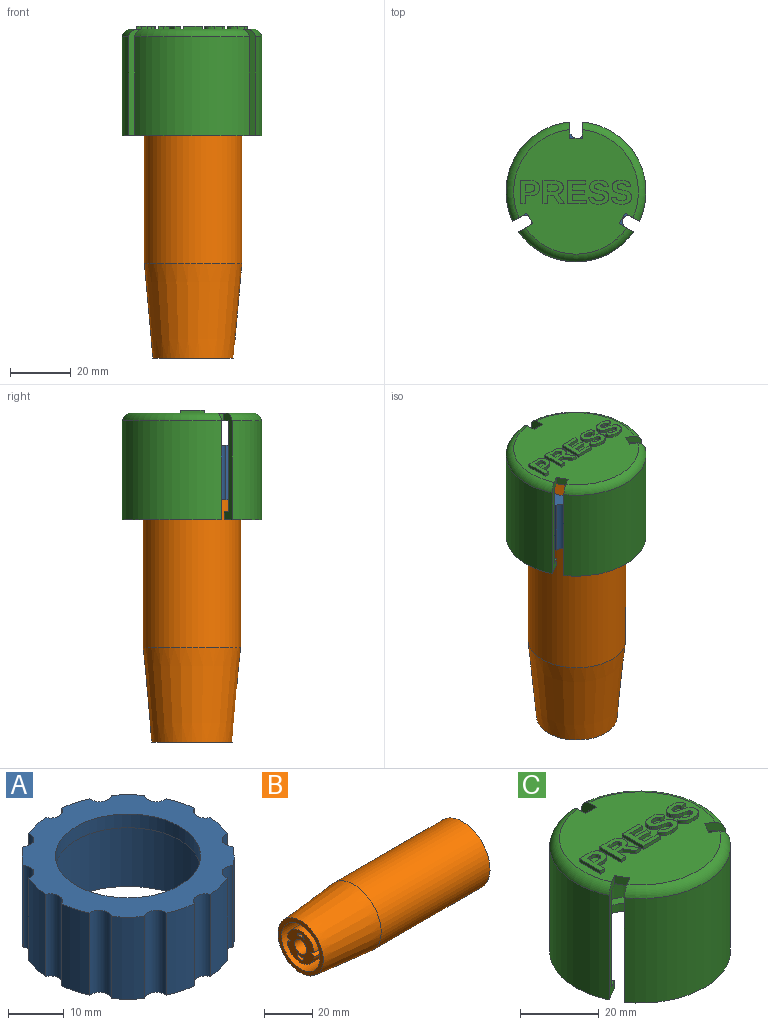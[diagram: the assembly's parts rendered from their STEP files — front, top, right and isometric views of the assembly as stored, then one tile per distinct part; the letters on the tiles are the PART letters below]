
ASSEMBLY  parts=3 mates=1
PART A: 29 faces, bbox 37.8x37.8x18 mm
  f0: plane 32x32mm, normal (0,0,-1), area 273.3mm2, adj f25,f27
  f1: cylinder r=2.13mm len=18mm, axis (0,0,-1), area 93.4mm2, adj f2,f24,f26,f28
  f2: cylinder r=19mm len=18mm, axis (0,0,-1), area 106.9mm2, adj f1,f3,f26,f28
  f3: cylinder r=2.13mm len=18mm, axis (0,0,-1), area 93.4mm2, adj f2,f4,f26,f28
  f4: cylinder r=19mm len=18mm, axis (0,0,-1), area 106.9mm2, adj f3,f5,f26,f28
  f5: cylinder r=2.13mm len=18mm, axis (0,0,-1), area 93.4mm2, adj f4,f6,f26,f28
  f6: cylinder r=19mm len=18mm, axis (0,0,-1), area 106.9mm2, adj f5,f7,f26,f28
  f7: cylinder r=2.13mm len=18mm, axis (0,0,-1), area 93.4mm2, adj f6,f8,f26,f28
  f8: cylinder r=19mm len=18mm, axis (0,0,-1), area 106.9mm2, adj f7,f9,f26,f28
  f9: cylinder r=2.13mm len=18mm, axis (0,0,-1), area 93.4mm2, adj f8,f10,f26,f28
  f10: cylinder r=19mm len=18mm, axis (0,0,-1), area 106.9mm2, adj f9,f11,f26,f28
  f11: cylinder r=2.13mm len=18mm, axis (0,0,-1), area 93.4mm2, adj f10,f12,f26,f28
  f12: cylinder r=19mm len=18mm, axis (0,0,-1), area 106.9mm2, adj f11,f13,f26,f28
  f13: cylinder r=2.13mm len=18mm, axis (0,0,-1), area 93.4mm2, adj f12,f14,f26,f28
  f14: cylinder r=19mm len=18mm, axis (0,0,-1), area 106.9mm2, adj f13,f15,f26,f28
  f15: cylinder r=2.13mm len=18mm, axis (0,0,-1), area 93.4mm2, adj f14,f16,f26,f28
  f16: cylinder r=19mm len=18mm, axis (0,0,-1), area 106.9mm2, adj f15,f17,f26,f28
  f17: cylinder r=2.13mm len=18mm, axis (0,0,-1), area 93.4mm2, adj f16,f18,f26,f28
  f18: cylinder r=19mm len=18mm, axis (0,0,-1), area 106.9mm2, adj f17,f19,f26,f28
  f19: cylinder r=2.13mm len=18mm, axis (0,0,-1), area 93.4mm2, adj f18,f20,f26,f28
  f20: cylinder r=19mm len=18mm, axis (0,0,-1), area 106.9mm2, adj f19,f21,f26,f28
  f21: cylinder r=2.13mm len=18mm, axis (0,0,-1), area 93.4mm2, adj f20,f22,f26,f28
  f22: cylinder r=19mm len=18mm, axis (0,0,-1), area 106.9mm2, adj f21,f23,f26,f28
  f23: cylinder r=2.13mm len=18mm, axis (0,0,-1), area 93.4mm2, adj f22,f24,f26,f28
  f24: cylinder r=19mm len=18mm, axis (0,0,-1), area 106.9mm2, adj f1,f23,f26,f28
  f25: cylinder r=13mm len=26mm, axis (0,0,-1), area 245mm2, adj f0,f26
  f26: plane 37.79x37.79mm, normal (0,0,1), area 551.1mm2, adj f1,f2,f3,f4,f5,f6,f7,f8
  f27: cylinder r=16mm len=32mm, axis (0,0,1), area 1508mm2, adj f0,f28
  f28: plane 37.79x37.79mm, normal (0,0,-1), area 277.8mm2, adj f1,f2,f3,f4,f5,f6,f7,f8
PART B: 31 faces, bbox 94.5x32x32 mm
  f0: cylinder r=5mm len=13mm, axis (-1,0,0), area 150.7mm2, adj f2,f25,f26,f30
  f1: cylinder r=5mm len=13mm, axis (-1,0,0), area 150.7mm2, adj f2,f25,f26,f30
  f2: plane 22x22mm, normal (1,0,0), area 291.9mm2, adj f0,f1,f10,f25,f26
  f3: plane 16x15.85mm, normal (-1,0,0), area 148.4mm2, adj f4,f11,f21,f22,f23,f24,f25,f26
  f4: cylinder r=8mm len=15.85mm, axis (-1,0,0), area 343.6mm2, adj f3,f12,f21,f23
  f5: plane 25.9x13mm, normal (1,0,0), area 73.1mm2, adj f7,f10,f17,f19
  f6: cylinder r=13mm len=63.5mm, axis (-1,0,0), area 2450.1mm2, adj f8,f9,f18,f20
  f7: cylinder r=13mm len=63.5mm, axis (-1,0,0), area 2450.1mm2, adj f5,f9,f17,f19
  f8: plane 25.9x13mm, normal (1,0,0), area 73.1mm2, adj f6,f10,f18,f20
  f9: plane 32x32mm, normal (1,0,0), area 277.9mm2, adj f6,f7,f16,f17,f18,f19,f20
  f10: cylinder r=11mm len=22mm, axis (-1,0,0), area 898.5mm2, adj f2,f5,f8
  f11: cylinder r=8mm len=15.85mm, axis (-1,0,0), area 343.6mm2, adj f3,f12,f22,f24
  f12: plane 22.4x22.4mm, normal (-1,0,0), area 197.5mm2, adj f4,f11,f13,f21,f22,f23,f24
  f13: cylinder r=11.2mm len=22.4mm, axis (-1,0,0), area 1055.6mm2, adj f12,f14
  f14: plane 26.4x26.4mm, normal (-1,0,0), area 153.3mm2, adj f13,f15
  f15: cone r=13.2mm half-angle=5.2deg, axis (1,0,0), area 2855.3mm2, adj f14,f16
  f16: cylinder r=16mm len=63.5mm, axis (-1,0,0), area 6383.7mm2, adj f9,f15
  f17: plane 63.5x1.95mm, normal (0,0.5,0.87), area 143.1mm2, adj f5,f7,f9,f18
  f18: plane 63.5x1.95mm, normal (0,0.5,-0.87), area 143.1mm2, adj f6,f8,f9,f17
  f19: plane 63.5x1.95mm, normal (0,-0.5,0.87), area 143.1mm2, adj f5,f7,f9,f20
  f20: plane 63.5x1.95mm, normal (0,-0.5,-0.87), area 143.1mm2, adj f6,f8,f9,f19
  f21: plane 15x1.92mm, normal (0,0.5,0.87), area 33.3mm2, adj f3,f4,f12,f22
  f22: plane 15x1.92mm, normal (0,0.5,-0.87), area 33.3mm2, adj f3,f11,f12,f21
  f23: plane 15x1.92mm, normal (0,-0.5,0.87), area 33.3mm2, adj f3,f4,f12,f24
  f24: plane 15x1.92mm, normal (0,-0.5,-0.87), area 33.3mm2, adj f3,f11,f12,f23
  f25: cylinder r=2mm len=18mm, axis (-1,0,0), area 110.2mm2, adj f0,f1,f2,f3,f27
  f26: cylinder r=2mm len=18mm, axis (-1,0,0), area 110.2mm2, adj f0,f1,f2,f3,f28
  f27: cylinder r=5mm len=5mm, axis (-1,0,0), area 20.6mm2, adj f3,f25,f30
  f28: cylinder r=5mm len=5mm, axis (-1,0,0), area 20.6mm2, adj f3,f26,f30
  f29: cylinder r=3.5mm len=7mm, axis (-1,0,0), area 110mm2, adj f3,f30
  f30: plane 10x10mm, normal (1,0,0), area 40.1mm2, adj f0,f1,f27,f28,f29
PART C: 147 faces, bbox 50.1x50x36 mm
  f0: plane 41x40.9mm, normal (0,0,1), area 1130.9mm2, adj f16,f17,f18,f22,f23,f24,f25,f26
  f1: plane 41x40.9mm, normal (0,0,-1), area 1001.1mm2, adj f2,f3,f4,f20,f22,f23,f24,f25
  f2: cylinder r=20.5mm len=30mm, axis (0,0,-1), area 1167.9mm2, adj f1,f5,f23,f28
  f3: cylinder r=20.5mm len=30mm, axis (0,0,-1), area 1167.9mm2, adj f1,f6,f25,f30
  f4: cylinder r=20.5mm len=33.34mm, axis (0,0,-1), area 1167.9mm2, adj f1,f7,f22,f26
  f5: plane 28.87x18.5mm, normal (0,0,1), area 90.8mm2, adj f2,f8,f23,f28
  f6: plane 28.87x18.5mm, normal (0,0,1), area 90.8mm2, adj f3,f9,f25,f30
  f7: plane 33.34x9.82mm, normal (0,0,1), area 90.8mm2, adj f4,f10,f22,f26
  f8: cylinder r=18mm len=25.1mm, axis (0,0,-1), area 84.2mm2, adj f5,f21,f23,f28
  f9: cylinder r=18mm len=25.1mm, axis (0,0,-1), area 84.2mm2, adj f6,f11,f25,f30
  f10: cylinder r=18mm len=28.98mm, axis (0,0,-1), area 84.2mm2, adj f7,f12,f22,f26
  f11: plane 32.64x21mm, normal (0,0,-1), area 194.6mm2, adj f9,f14,f25,f30
  f12: plane 37.69x12.32mm, normal (0,0,-1), area 194.6mm2, adj f10,f15,f22,f26
  f13: cylinder r=23mm len=32.64mm, axis (0,0,-1), area 1435.4mm2, adj f16,f21,f23,f28
  f14: cylinder r=23mm len=32.64mm, axis (0,0,-1), area 1435.4mm2, adj f11,f17,f25,f30
  f15: cylinder r=23mm len=37.69mm, axis (0,0,-1), area 1435.4mm2, adj f12,f18,f22,f26
  f16: torus R=19.57mm, axis (0,0,-1), area 155.5mm2, adj f0,f13,f23,f28
  f17: torus R=19.57mm, axis (0,0,-1), area 155.5mm2, adj f0,f14,f25,f30
  f18: torus R=19.57mm, axis (0,0,-1), area 155.5mm2, adj f0,f15,f22,f26
  f19: torus R=0.2mm, axis (0,0,-1), area 167.1mm2, adj f146
  f20: cone r=8.27mm half-angle=10deg, axis (0,0,1), area 341.2mm2, adj f1,f146
  f21: plane 32.64x21mm, normal (0,0,-1), area 194.6mm2, adj f8,f13,f23,f28
  f22: plane 35x4.69mm, normal (0.5,0.87,0), area 99.4mm2, adj f0,f1,f4,f7,f10,f12,f15,f18
  f23: plane 35x4.69mm, normal (-0.5,-0.87,0), area 99.4mm2, adj f0,f1,f2,f5,f8,f13,f16,f21
  f24: plane 3.46x2.5mm, normal (0.87,-0.5,0), area 10mm2, adj f0,f1,f22,f23
  f25: plane 35x4.69mm, normal (0.5,-0.87,0), area 99.4mm2, adj f0,f1,f3,f6,f9,f11,f14,f17
  f26: plane 35x4.69mm, normal (-0.5,0.87,0), area 99.4mm2, adj f0,f1,f4,f7,f10,f12,f15,f18
  f27: plane 3.46x2.5mm, normal (-0.87,-0.5,0), area 10mm2, adj f0,f1,f25,f26
  f28: plane 35x5.42mm, normal (-1,0,0), area 99.4mm2, adj f0,f1,f2,f5,f8,f13,f16,f21
  f29: plane 4x2.5mm, normal (0,1,0), area 10mm2, adj f0,f1,f28,f30
  f30: plane 35x5.42mm, normal (1,0,0), area 99.4mm2, adj f0,f1,f3,f6,f9,f11,f14,f17
  f31: extruded ~1.42x1.21mm, area 2.1mm2, adj f32,f46,f47,f48
  f32: extruded ~1x0.95mm, area 1mm2, adj f31,f33,f47,f48
  f33: extruded ~1.02x1mm, area 1.1mm2, adj f32,f34,f47,f48
  f34: plane 1.7x1mm, normal (0,1,0), area 1.7mm2, adj f33,f35,f47,f48
  f35: plane 2.48x1mm, normal (1,0,0), area 2.5mm2, adj f34,f46,f47,f48
  f36: extruded ~1.32x1mm, area 1.4mm2, adj f0,f37,f45,f47
  f37: extruded ~1.79x1mm, area 2mm2, adj f0,f36,f38,f47
  f38: extruded ~2.11x1mm, area 2.3mm2, adj f0,f37,f39,f47
  f39: plane 3.43x1mm, normal (0,1,0), area 3.4mm2, adj f0,f38,f40,f47
  f40: plane 7.64x1mm, normal (-1,0,0), area 7.6mm2, adj f0,f39,f41,f47
  f41: plane 1.6x1mm, normal (0,-1,0), area 1.6mm2, adj f0,f40,f42,f47
  f42: plane 2.69x1mm, normal (1,0,0), area 2.7mm2, adj f0,f41,f43,f47
  f43: plane 1.9x1mm, normal (0,-1,0), area 1.9mm2, adj f0,f42,f44,f47
  f44: extruded ~1.49x1mm, area 1.5mm2, adj f0,f43,f45,f47
  f45: extruded ~1x0.96mm, area 1.3mm2, adj f0,f36,f44,f47
  f46: plane 1.65x1mm, normal (0,-1,0), area 1.7mm2, adj f31,f35,f47,f48
  f47: plane 7.64x6.29mm, normal (0,0,1), area 25.8mm2, adj f31,f32,f33,f34,f35,f36,f37,f38
  f48: plane 3.08x2.48mm, normal (0,0,1), area 7mm2, adj f31,f32,f33,f34,f35,f46
  f49: extruded ~1.41x1.1mm, area 2mm2, adj f50,f66,f67,f68
  f50: extruded ~1x0.85mm, area 0.9mm2, adj f49,f51,f67,f68
  f51: extruded ~1.02x1mm, area 1.1mm2, adj f50,f52,f67,f68
  f52: plane 2.09x1mm, normal (0,1,0), area 2.1mm2, adj f51,f53,f67,f68
  f53: plane 2.26x1mm, normal (1,0,0), area 2.3mm2, adj f52,f66,f67,f68
  f54: plane 2.9x1.77mm, normal (-0.85,-0.52,0), area 3.4mm2, adj f0,f55,f65,f67
  f55: plane 1.8x1mm, normal (0,-1,0), area 1.8mm2, adj f0,f54,f56,f67
  f56: plane 3.21x2.07mm, normal (0.84,0.54,0), area 3.8mm2, adj f0,f55,f57,f67
  f57: extruded ~1.23x1mm, area 1.5mm2, adj f0,f56,f58,f67
  f58: extruded ~1.39x1mm, area 1.5mm2, adj f0,f57,f59,f67
  f59: extruded ~1.69x1mm, area 1.9mm2, adj f0,f58,f60,f67
  f60: extruded ~2.11x1mm, area 2.2mm2, adj f0,f59,f61,f67
  f61: plane 3.82x1mm, normal (0,1,0), area 3.8mm2, adj f0,f60,f62,f67
  f62: plane 7.64x1mm, normal (-1,0,0), area 7.6mm2, adj f0,f61,f63,f67
  f63: plane 1.6x1mm, normal (0,-1,0), area 1.6mm2, adj f0,f62,f64,f67
  f64: plane 2.9x1mm, normal (1,0,0), area 2.9mm2, adj f0,f63,f65,f67
  f65: plane 1.88x1mm, normal (0,-1,0), area 1.9mm2, adj f0,f54,f64,f67
  f66: plane 2.05x1mm, normal (0,-1,0), area 2.1mm2, adj f49,f53,f67,f68
  f67: plane 7.64x7.05mm, normal (0,0,1), area 31.6mm2, adj f49,f50,f51,f52,f53,f54,f55,f56
  f68: plane 3.46x2.26mm, normal (0,0,1), area 7.3mm2, adj f49,f50,f51,f52,f53,f66
  f69: plane 7.64x1mm, normal (-1,0,0), area 7.6mm2, adj f0,f70,f80,f81
  f70: plane 6.23x1mm, normal (0,-1,0), area 6.2mm2, adj f0,f69,f71,f81
  f71: plane 1.24x1mm, normal (1,0,0), area 1.2mm2, adj f0,f70,f72,f81
  f72: plane 4.63x1mm, normal (0,1,0), area 4.6mm2, adj f0,f71,f73,f81
  f73: plane 2.01x1mm, normal (1,0,0), area 2mm2, adj f0,f72,f74,f81
  f74: plane 4.08x1mm, normal (0,-1,0), area 4.1mm2, adj f0,f73,f75,f81
  f75: plane 1.24x1mm, normal (1,0,0), area 1.2mm2, adj f0,f74,f76,f81
  f76: plane 4.08x1mm, normal (0,1,0), area 4.1mm2, adj f0,f75,f77,f81
  f77: plane 1.92x1mm, normal (1,0,0), area 1.9mm2, adj f0,f76,f78,f81
  f78: plane 4.41x1mm, normal (0,-1,0), area 4.4mm2, adj f0,f77,f79,f81
  f79: plane 1.24x1mm, normal (1,0,0), area 1.2mm2, adj f0,f78,f80,f81
  f80: plane 6.01x1mm, normal (0,1,0), area 6mm2, adj f0,f69,f79,f81
  f81: plane 7.64x6.23mm, normal (0,0,1), area 28.5mm2, adj f69,f70,f71,f72,f73,f74,f75,f76
  f82: extruded ~1.72x1mm, area 2mm2, adj f0,f83,f112,f113
  f83: extruded ~1x0.84mm, area 0.9mm2, adj f0,f82,f84,f113
  f84: extruded ~1x0.63mm, area 0.8mm2, adj f0,f83,f85,f113
  f85: extruded ~1x0.75mm, area 0.9mm2, adj f0,f84,f86,f113
  f86: extruded ~1.58x1mm, area 1.6mm2, adj f0,f85,f87,f113
  f87: extruded ~1.23x1mm, area 1.3mm2, adj f0,f86,f88,f113
  f88: extruded ~1x0.46mm, area 0.6mm2, adj f0,f87,f89,f113
  f89: extruded ~1x0.49mm, area 0.5mm2, adj f0,f88,f90,f113
  f90: extruded ~1.45x1mm, area 1.9mm2, adj f0,f89,f91,f113
  f91: extruded ~1.05x1mm, area 1.1mm2, adj f0,f90,f92,f113
  f92: extruded ~1x0.74mm, area 0.9mm2, adj f0,f91,f93,f113
  f93: plane 1.55x1mm, normal (0.14,-0.99,0), area 1.6mm2, adj f0,f92,f94,f113
  f94: extruded ~1.47x1mm, area 1.8mm2, adj f0,f93,f95,f113
  f95: extruded ~2.13x1mm, area 2.2mm2, adj f0,f94,f96,f113
  f96: extruded ~2.26x1mm, area 2.4mm2, adj f0,f95,f97,f113
  f97: extruded ~1.59x1mm, area 1.8mm2, adj f0,f96,f98,f113
  f98: extruded ~1x0.72mm, area 0.7mm2, adj f0,f97,f99,f113
  f99: extruded ~1x0.55mm, area 0.6mm2, adj f0,f98,f100,f113
  f100: extruded ~1x0.46mm, area 0.6mm2, adj f0,f99,f101,f113
  f101: extruded ~1x0.61mm, area 0.7mm2, adj f0,f100,f102,f113
  f102: extruded ~1.19x1mm, area 1.2mm2, adj f0,f101,f103,f113
  f103: extruded ~1.34x1mm, area 1.4mm2, adj f0,f102,f104,f113
  f104: extruded ~1x0.54mm, area 0.7mm2, adj f0,f103,f105,f113
  f105: extruded ~1x0.54mm, area 0.6mm2, adj f0,f104,f106,f113
  f106: extruded ~1.68x1.02mm, area 2.2mm2, adj f0,f105,f107,f113
  f107: extruded ~1.26x1mm, area 1.3mm2, adj f0,f106,f108,f113
  f108: extruded ~1x0.88mm, area 1.1mm2, adj f0,f107,f109,f113
  f109: plane 1.55x1mm, normal (-0.16,0.99,0), area 1.6mm2, adj f0,f108,f110,f113
  f110: extruded ~1.58x1.07mm, area 2mm2, adj f0,f109,f111,f113
  f111: extruded ~2.31x1mm, area 2.4mm2, adj f0,f110,f112,f113
  f112: extruded ~2.44x1mm, area 2.6mm2, adj f0,f82,f111,f113
  f113: plane 7.87x6.66mm, normal (0,0,1), area 26.8mm2, adj f82,f83,f84,f85,f86,f87,f88,f89
  f114: extruded ~1.72x1mm, area 2mm2, adj f0,f115,f144,f145
  f115: extruded ~1x0.84mm, area 0.9mm2, adj f0,f114,f116,f145
  f116: extruded ~1x0.63mm, area 0.8mm2, adj f0,f115,f117,f145
  f117: extruded ~1x0.75mm, area 0.9mm2, adj f0,f116,f118,f145
  f118: extruded ~1.58x1mm, area 1.6mm2, adj f0,f117,f119,f145
  f119: extruded ~1.23x1mm, area 1.3mm2, adj f0,f118,f120,f145
  f120: extruded ~1x0.46mm, area 0.6mm2, adj f0,f119,f121,f145
  f121: extruded ~1x0.49mm, area 0.5mm2, adj f0,f120,f122,f145
  f122: extruded ~1.45x1mm, area 1.9mm2, adj f0,f121,f123,f145
  f123: extruded ~1.05x1mm, area 1.1mm2, adj f0,f122,f124,f145
  f124: extruded ~1x0.74mm, area 0.9mm2, adj f0,f123,f125,f145
  f125: plane 1.55x1mm, normal (0.14,-0.99,0), area 1.6mm2, adj f0,f124,f126,f145
  f126: extruded ~1.47x1mm, area 1.8mm2, adj f0,f125,f127,f145
  f127: extruded ~2.13x1mm, area 2.2mm2, adj f0,f126,f128,f145
  f128: extruded ~2.26x1mm, area 2.4mm2, adj f0,f127,f129,f145
  f129: extruded ~1.59x1mm, area 1.8mm2, adj f0,f128,f130,f145
  f130: extruded ~1x0.72mm, area 0.7mm2, adj f0,f129,f131,f145
  f131: extruded ~1x0.55mm, area 0.6mm2, adj f0,f130,f132,f145
  f132: extruded ~1x0.46mm, area 0.6mm2, adj f0,f131,f133,f145
  f133: extruded ~1x0.61mm, area 0.7mm2, adj f0,f132,f134,f145
  f134: extruded ~1.19x1mm, area 1.2mm2, adj f0,f133,f135,f145
  f135: extruded ~1.34x1mm, area 1.4mm2, adj f0,f134,f136,f145
  f136: extruded ~1x0.54mm, area 0.7mm2, adj f0,f135,f137,f145
  f137: extruded ~1x0.54mm, area 0.6mm2, adj f0,f136,f138,f145
  f138: extruded ~1.68x1.02mm, area 2.2mm2, adj f0,f137,f139,f145
  f139: extruded ~1.26x1mm, area 1.3mm2, adj f0,f138,f140,f145
  f140: extruded ~1x0.88mm, area 1.1mm2, adj f0,f139,f141,f145
  f141: plane 1.55x1mm, normal (-0.16,0.99,0), area 1.6mm2, adj f0,f140,f142,f145
  f142: extruded ~1.58x1.07mm, area 2mm2, adj f0,f141,f143,f145
  f143: extruded ~2.31x1mm, area 2.4mm2, adj f0,f142,f144,f145
  f144: extruded ~2.44x1mm, area 2.6mm2, adj f0,f114,f143,f145
  f145: plane 7.87x6.66mm, normal (0,0,1), area 26.8mm2, adj f114,f115,f116,f117,f118,f119,f120,f121
  f146: torus R=7.46mm, axis (0,0,1), area 80.6mm2, adj f19,f20
PLACE A t=(-37.2,-32.47,-10.49)mm
PLACE B rot(axis=(0,-1,0),90deg) t=(-37.2,-32.47,-60.49)mm
PLACE C t=(-37.57,-32.47,-14.45)mm
MATE fastened B.f0 <-> A.f27  axis (0,0,1) through (-37.2,-32.47,-10.49)mm
